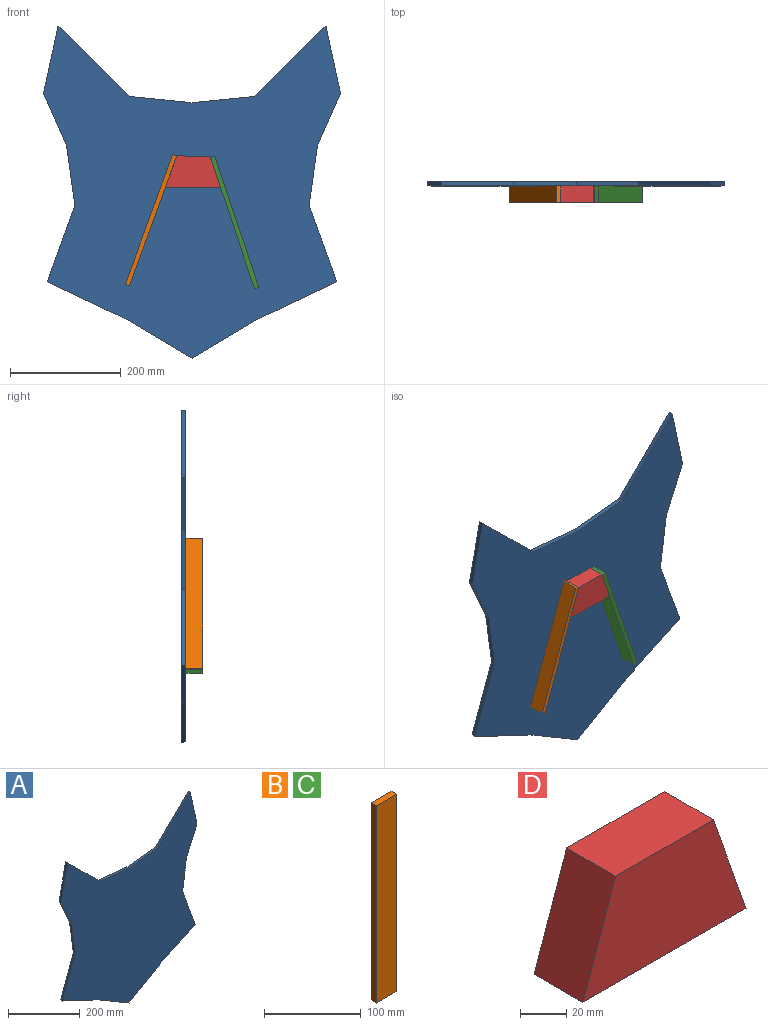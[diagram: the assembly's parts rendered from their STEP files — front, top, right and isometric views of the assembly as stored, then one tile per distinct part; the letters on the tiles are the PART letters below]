
ASSEMBLY  parts=4 mates=5
PART A: 18 faces, bbox 536.9x8x600 mm
  f0: plane 94.52x41.77mm, normal (-0.91,0,-0.4), area 830.5mm2, adj f1,f15,f16,f17
  f1: plane 108.75x14.92mm, normal (-0.99,0,-0.14), area 882.1mm2, adj f0,f2,f16,f17
  f2: plane 137.55x49.78mm, normal (-0.94,0,0.34), area 1175.6mm2, adj f1,f3,f16,f17
  f3: plane 142.43x67.1mm, normal (-0.43,0,-0.9), area 1265.3mm2, adj f2,f4,f16,f17
  f4: plane 119.1x70.39mm, normal (-0.51,0,-0.86), area 1111.8mm2, adj f3,f5,f16,f17
  f5: plane 119.1x70.39mm, normal (0.51,0,-0.86), area 1111.8mm2, adj f4,f6,f16,f17
  f6: plane 142.43x67.1mm, normal (0.43,0,-0.9), area 1265.3mm2, adj f5,f7,f16,f17
  f7: plane 137.55x49.78mm, normal (0.94,0,0.34), area 1175.6mm2, adj f6,f8,f16,f17
  f8: plane 108.75x14.92mm, normal (0.99,0,-0.14), area 882.1mm2, adj f7,f9,f16,f17
  f9: plane 94.52x41.77mm, normal (0.91,0,-0.4), area 830.5mm2, adj f8,f10,f16,f17
  f10: plane 121.69x26.27mm, normal (0.98,0,0.21), area 1000.4mm2, adj f9,f11,f16,f17
  f11: plane 128.6x127.22mm, normal (-0.7,0,0.71), area 1453.7mm2, adj f10,f12,f16,f17
  f12: plane 113.57x11.37mm, normal (-0.1,0,1), area 917.3mm2, adj f11,f13,f16,f17
  f13: plane 113.57x11.37mm, normal (0.1,0,1), area 917.3mm2, adj f12,f14,f16,f17
  f14: plane 128.6x127.22mm, normal (0.7,0,0.71), area 1453.7mm2, adj f13,f15,f16,f17
  f15: plane 121.69x26.27mm, normal (-0.98,0,0.21), area 1000.4mm2, adj f0,f14,f16,f17
  f16: plane 600x536.89mm, normal (0,1,0), area 209088.9mm2, adj f0,f1,f2,f3,f4,f5,f6,f7
  f17: plane 600x536.89mm, normal (0,-1,0), area 209088.9mm2, adj f0,f1,f2,f3,f4,f5,f6,f7
PART B: 6 faces, bbox 30x8x250 mm
  f0: plane 250x8mm, normal (-1,0,0), area 2000mm2, adj f1,f3,f4,f5
  f1: plane 30x8mm, normal (0,0,-1), area 240mm2, adj f0,f2,f4,f5
  f2: plane 250x8mm, normal (1,0,0), area 2000mm2, adj f1,f3,f4,f5
  f3: plane 30x8mm, normal (0,0,1), area 240mm2, adj f0,f2,f4,f5
  f4: plane 250x30mm, normal (0,-1,0), area 7500mm2, adj f0,f1,f2,f3
  f5: plane 250x30mm, normal (0,1,0), area 7500mm2, adj f0,f1,f2,f3
PART C: same geometry as B
PART D: 6 faces, bbox 100x30x57.1 mm
  f0: plane 57.06x30mm, normal (-0.94,0,0.33), area 1813.9mm2, adj f1,f3,f4,f5
  f1: plane 100x30mm, normal (0,0,-1), area 3000mm2, adj f0,f2,f4,f5
  f2: plane 57.06x30mm, normal (0.94,0,0.33), area 1813.9mm2, adj f1,f3,f4,f5
  f3: plane 60x30mm, normal (0,0,1), area 1800mm2, adj f0,f2,f4,f5
  f4: plane 100x57.06mm, normal (0,-1,0), area 4564.7mm2, adj f0,f1,f2,f3
  f5: plane 100x57.06mm, normal (0,1,0), area 4564.7mm2, adj f0,f1,f2,f3
PLACE A t=(-206.04,3.47,36.4)mm
PLACE B rot(axis=(-0.17,0.17,-0.97),91.7deg) t=(-319.05,-4.57,-62.33)mm
PLACE C rot(axis=(0.16,-0.16,-0.97),91.5deg) t=(-85.12,-4.57,-65.53)mm
PLACE D rot(axis=(0,1,0),0.7deg) t=(-254.26,-4.57,115.68)mm
MATE planar C.f0 <-> A.f17  axis (0,1,0) through (-128.85,-4.57,51.64)mm
MATE planar A.f17 <-> D.f5  axis (0,-1,0) through (-206.04,-4.57,97.1)mm
MATE planar B.f0 <-> A.f17  axis (0,1,0) through (-233.54,-4.57,172.59)mm
MATE planar D.f0 <-> B.f5  axis (-0.94,0,0.34) through (-243.92,-19.57,144.09)mm
MATE planar C.f4 <-> D.f2  axis (-0.95,0,-0.32) through (-132.64,-19.57,50.36)mm
